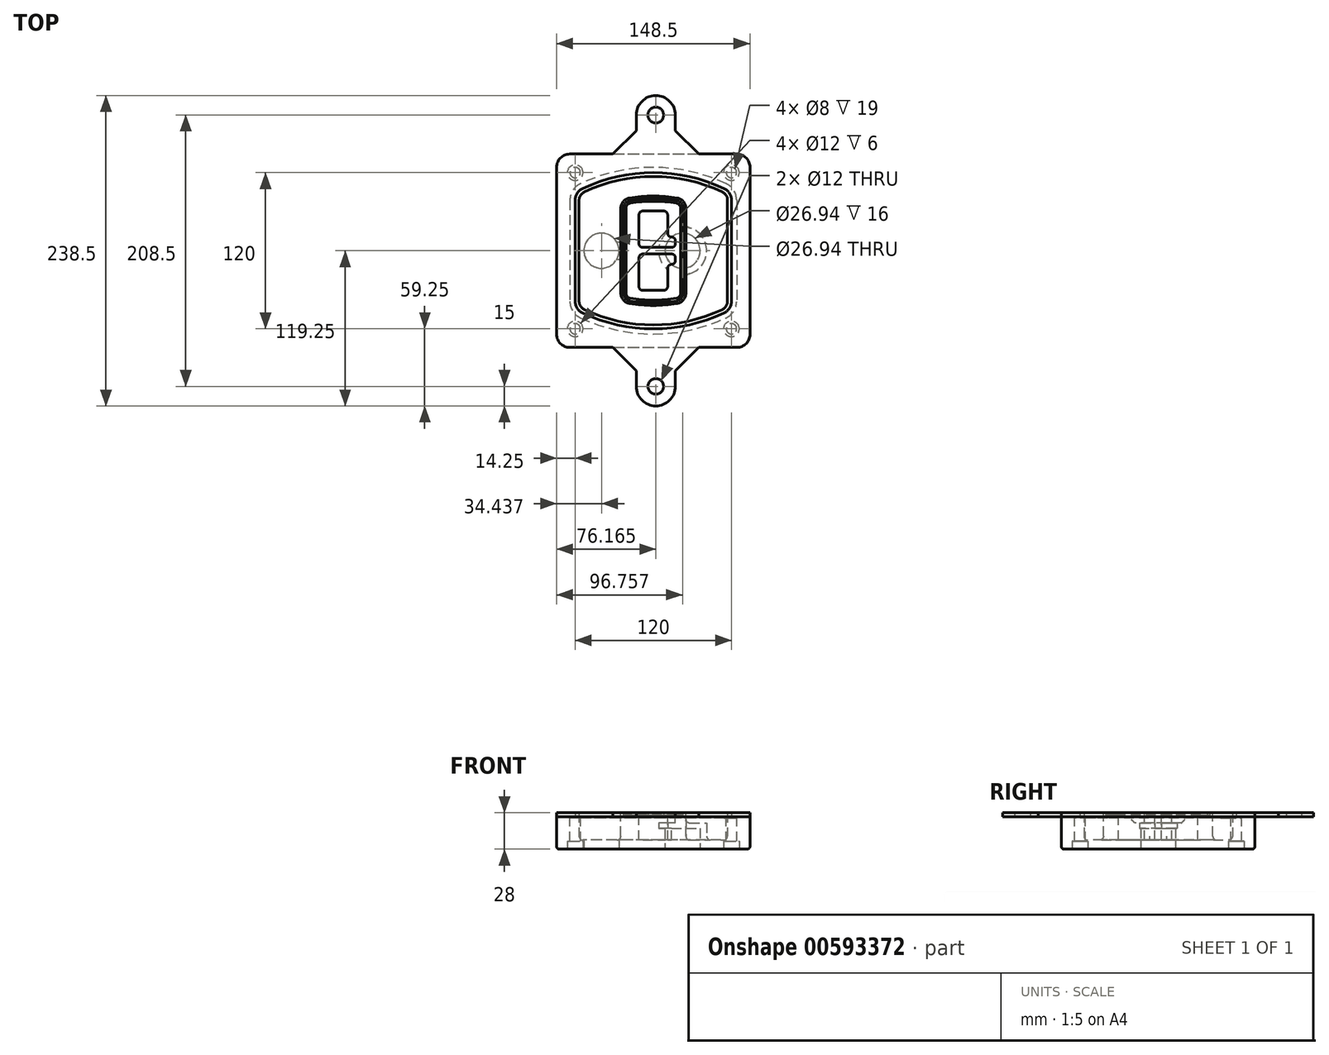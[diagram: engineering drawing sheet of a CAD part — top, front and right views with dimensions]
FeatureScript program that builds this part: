
annotation { "Feature Type Name" : "Feature", "Feature Type Description" : "" }
export const myFeature = defineFeature(function(context is Context, id is Id, definition is map)
    precondition{}
    {
        {
            var Q0;
            Q0=qCreatedBy(makeId("Top.planeOp"),FACE);
            var sketch = newSketch(context, id + "F0", { "sketchPlane" : qUnion([Q0])});
            skPoint(sketch, "E0.rect.middle", {"position": v(0, 0) * mm});
            skLineSegment(sketch, "E1.bottom", {"start": v(-64.25, -74.25) * mm, "end": v(64.25, -74.25) * mm});
            skLineSegment(sketch, "E1.top", {"start": v(-64.25, 74.25) * mm, "end": v(64.25, 74.25) * mm});
            skLineSegment(sketch, "E1.left", {"start": v(-74.25, -64.25) * mm, "end": v(-74.25, 64.25) * mm});
            skLineSegment(sketch, "E1.right", {"start": v(74.25, -64.25) * mm, "end": v(74.25, 64.25) * mm});
            skLineSegment(sketch, "E2", {"start": v(-74.25, 74.25) * mm, "end": v(74.25, -74.25) * mm, "construction": true});
            skLineSegment(sketch, "E3", {"start": v(74.25, 74.25) * mm, "end": v(-74.25, -74.25) * mm, "construction": true});
            skCircle(sketch, "E4", {"center": v(-60, 60) * mm, "radius": 4 * mm});
            skCircle(sketch, "E5", {"center": v(60, 60) * mm, "radius": 4 * mm});
            skCircle(sketch, "E6", {"center": v(60, -60) * mm, "radius": 4 * mm});
            skCircle(sketch, "E7", {"center": v(-60, -60) * mm, "radius": 4 * mm});
            skLineSegment(sketch, "E8", {"start": v(-60, 60) * mm, "end": v(60, 60) * mm, "construction": true});
            skLineSegment(sketch, "E9", {"start": v(60, 60) * mm, "end": v(60, -60) * mm, "construction": true});
            skLineSegment(sketch, "E10", {"start": v(60, -60) * mm, "end": v(-60, -60) * mm, "construction": true});
            skLineSegment(sketch, "E11", {"start": v(-60, -60) * mm, "end": v(-60, 60) * mm, "construction": true});
            skLineSegment(sketch, "E12", {"start": v(-60, 38.83) * mm, "end": v(-60, -38.83) * mm});
            skLineSegment(sketch, "E13", {"start": v(60, 38.83) * mm, "end": v(60, -38.83) * mm});
            skArc(sketch, "E14", {"start": v(54.26, 47.88) * mm, "mid": v(0, 60) * mm, "end": v(-54.26, 47.88) * mm});
            skArc(sketch, "E15", {"start": v(-54.26, -47.88) * mm, "mid": v(0, -60) * mm, "end": v(54.26, -47.88) * mm});
            skLineSegment(sketch, "E16", {"start": v(-60, 0) * mm, "end": v(60, 0) * mm, "construction": true});
            skPoint(sketch, "E17.visualSharp", {"position": v(-60, -45) * mm});
            skArc(sketch, "E17.filletArc", {"start": v(-60, -38.83) * mm, "mid": v(-58.44, -44.2) * mm, "end": v(-54.26, -47.88) * mm});
            skPoint(sketch, "E18.visualSharp", {"position": v(-60, 45) * mm});
            skArc(sketch, "E18.filletArc", {"start": v(-54.26, 47.88) * mm, "mid": v(-58.44, 44.2) * mm, "end": v(-60, 38.83) * mm});
            skPoint(sketch, "E19.visualSharp", {"position": v(60, 45) * mm});
            skArc(sketch, "E19.filletArc", {"start": v(60, 38.83) * mm, "mid": v(58.44, 44.2) * mm, "end": v(54.26, 47.88) * mm});
            skPoint(sketch, "E20.visualSharp", {"position": v(60, -45) * mm});
            skArc(sketch, "E20.filletArc", {"start": v(54.26, -47.88) * mm, "mid": v(58.44, -44.2) * mm, "end": v(60, -38.83) * mm});
            skPoint(sketch, "E21.visualSharp", {"position": v(-74.25, 74.25) * mm});
            skArc(sketch, "E21.filletArc", {"start": v(-64.25, 74.25) * mm, "mid": v(-71.32, 71.32) * mm, "end": v(-74.25, 64.25) * mm});
            skPoint(sketch, "E22.visualSharp", {"position": v(74.25, 74.25) * mm});
            skArc(sketch, "E22.filletArc", {"start": v(74.25, 64.25) * mm, "mid": v(71.32, 71.32) * mm, "end": v(64.25, 74.25) * mm});
            skPoint(sketch, "E23.visualSharp", {"position": v(74.25, -74.25) * mm});
            skArc(sketch, "E23.filletArc", {"start": v(64.25, -74.25) * mm, "mid": v(71.32, -71.32) * mm, "end": v(74.25, -64.25) * mm});
            skPoint(sketch, "E24.visualSharp", {"position": v(-74.25, -74.25) * mm});
            skArc(sketch, "E24.filletArc", {"start": v(-74.25, -64.25) * mm, "mid": v(-71.32, -71.32) * mm, "end": v(-64.25, -74.25) * mm});
            skArc(sketch, "E25.0", {"start": v(57, 38.83) * mm, "mid": v(55.9, 42.58) * mm, "end": v(52.98, 45.17) * mm});
            skLineSegment(sketch, "E25.1", {"start": v(57, 38.83) * mm, "end": v(57, -38.83) * mm});
            skArc(sketch, "E25.2", {"start": v(52.98, -45.17) * mm, "mid": v(55.9, -42.58) * mm, "end": v(57, -38.83) * mm});
            skArc(sketch, "E25.3", {"start": v(-52.98, -45.17) * mm, "mid": v(0, -57) * mm, "end": v(52.98, -45.17) * mm});
            skArc(sketch, "E25.4", {"start": v(-57, -38.83) * mm, "mid": v(-55.9, -42.58) * mm, "end": v(-52.98, -45.17) * mm});
            skArc(sketch, "E25.5", {"start": v(52.98, 45.17) * mm, "mid": v(0, 57) * mm, "end": v(-52.98, 45.17) * mm});
            skLineSegment(sketch, "E25.6", {"start": v(-57, 38.83) * mm, "end": v(-57, -38.83) * mm});
            skArc(sketch, "E25.7", {"start": v(-52.98, 45.17) * mm, "mid": v(-55.9, 42.58) * mm, "end": v(-57, 38.83) * mm});
            skArc(sketch, "E26.0", {"start": v(-55.96, 51.5) * mm, "mid": v(-61.82, 46.33) * mm, "end": v(-64, 38.83) * mm});
            skArc(sketch, "E26.1", {"start": v(55.96, 51.5) * mm, "mid": v(0, 64) * mm, "end": v(-55.96, 51.5) * mm});
            skArc(sketch, "E26.2", {"start": v(64, 38.83) * mm, "mid": v(61.82, 46.33) * mm, "end": v(55.96, 51.5) * mm});
            skLineSegment(sketch, "E26.3", {"start": v(64, 38.83) * mm, "end": v(64, -38.83) * mm});
            skArc(sketch, "E26.4", {"start": v(55.96, -51.5) * mm, "mid": v(61.82, -46.33) * mm, "end": v(64, -38.83) * mm});
            skLineSegment(sketch, "E26.5", {"start": v(-64, 38.83) * mm, "end": v(-64, -38.83) * mm});
            skArc(sketch, "E26.6", {"start": v(-55.96, -51.5) * mm, "mid": v(0, -64) * mm, "end": v(55.96, -51.5) * mm});
            skArc(sketch, "E26.7", {"start": v(-64, -38.83) * mm, "mid": v(-61.82, -46.33) * mm, "end": v(-55.96, -51.5) * mm});
            skSolve(sketch);
        }
        {
            var Q0;
            Q0=makeQuery(id+"F0.imprint","IMPRINT",FACE,{"disambiguationData":[TD([[makeQuery(id+"F0.imprint","IMPRINT",EDGE,{"derivedFrom":sQuery(id+"F0.wireOp",EDGE,"E1.bottom")}),1.0]])]});
            var Q1;
            Q1=makeQuery(id+"F0.imprint","IMPRINT",FACE,{"disambiguationData":[TD([[makeQuery(id+"F0.imprint","IMPRINT",EDGE,{"derivedFrom":sQuery(id+"F0.wireOp",EDGE,"E12")}),1.0]])]});
            var Q2;
            Q2=makeQuery(id+"F0.imprint","IMPRINT",FACE,{"disambiguationData":[TD([[makeQuery(id+"F0.imprint","IMPRINT",EDGE,{"derivedFrom":sQuery(id+"F0.wireOp",EDGE,"E25.0")}),1.0]])]});
            var Q3;
            Q3=makeQuery(id+"F0.imprint","IMPRINT",FACE,{"disambiguationData":[TD([[makeQuery(id+"F0.imprint","IMPRINT",EDGE,{"derivedFrom":sQuery(id+"F0.wireOp",EDGE,"E12")}),-1.0]])]});
            extrude(context, id + "F1", {"entities" : qUnion([Q0, Q1, Q2, Q3]), "oppositeDirection" : true, "depth" : 25 * mm});
        }
        {
            var Q0;
            Q0=makeQuery(id+"F0.imprint","IMPRINT",FACE,{"disambiguationData":[TD([[makeQuery(id+"F0.imprint","IMPRINT",EDGE,{"derivedFrom":sQuery(id+"F0.wireOp",EDGE,"E12")}),1.0]])]});
            extrude(context, id + "F2", {"entities" : qUnion([Q0]), "operationType" : NewBodyOperationType.ADD, "depth" : 3 * mm});
        }
        {
            var Q0;
            Q0=makeQuery(id+"F0.imprint","IMPRINT",FACE,{"disambiguationData":[TD([[makeQuery(id+"F0.imprint","IMPRINT",EDGE,{"derivedFrom":sQuery(id+"F0.wireOp",EDGE,"E12")}),-1.0]])]});
            extrude(context, id + "F3", {"entities" : qUnion([Q0]), "operationType" : NewBodyOperationType.REMOVE, "oppositeDirection" : true, "depth" : 1 * mm});
        }
        {
            var Q0;
            Q0=makeQuery(id+"F0.imprint","IMPRINT",FACE,{"disambiguationData":[TD([[makeQuery(id+"F0.imprint","IMPRINT",EDGE,{"derivedFrom":sQuery(id+"F0.wireOp",EDGE,"E25.0")}),1.0]])]});
            extrude(context, id + "F4", {"entities" : qUnion([Q0]), "operationType" : NewBodyOperationType.REMOVE, "oppositeDirection" : true, "depth" : 18 * mm});
        }
        {
            var Q0;
            Q0=makeQuery(id+"F2.opExtrude","CAP_FACE",FACE,{"disambiguationData":[OSD([sQuery(id+"F0.wireOp",EDGE,"E12"),sQuery(id+"F0.wireOp",EDGE,"E13"),sQuery(id+"F0.wireOp",EDGE,"E14"),sQuery(id+"F0.wireOp",EDGE,"E15"),sQuery(id+"F0.wireOp",EDGE,"E17.filletArc"),sQuery(id+"F0.wireOp",EDGE,"E18.filletArc"),sQuery(id+"F0.wireOp",EDGE,"E19.filletArc"),sQuery(id+"F0.wireOp",EDGE,"E20.filletArc"),sQuery(id+"F0.wireOp",EDGE,"E25.0"),sQuery(id+"F0.wireOp",EDGE,"E25.1"),sQuery(id+"F0.wireOp",EDGE,"E25.2"),sQuery(id+"F0.wireOp",EDGE,"E25.3"),sQuery(id+"F0.wireOp",EDGE,"E25.4"),sQuery(id+"F0.wireOp",EDGE,"E25.5"),sQuery(id+"F0.wireOp",EDGE,"E25.6"),sQuery(id+"F0.wireOp",EDGE,"E25.7")])],"isStart":false});
            var sketch = newSketch(context, id + "F5", { "sketchPlane" : qUnion([Q0])});
            skArc(sketch, "E27.0", {"start": v(-18.34, -40.45) * mm, "mid": v(0, -42) * mm, "end": v(18.34, -40.45) * mm});
            skArc(sketch, "E28.0", {"start": v(18.34, 40.45) * mm, "mid": v(0, 42) * mm, "end": v(-18.34, 40.45) * mm});
            skLineSegment(sketch, "E29", {"start": v(-25, 32.57) * mm, "end": v(-25, -32.57) * mm});
            skLineSegment(sketch, "E30", {"start": v(25, 32.57) * mm, "end": v(25, -32.57) * mm});
            skLineSegment(sketch, "E31", {"start": v(-25, 39.1) * mm, "end": v(25, 39.1) * mm, "construction": true});
            skLineSegment(sketch, "E32", {"start": v(-25, -39.1) * mm, "end": v(25, -39.1) * mm, "construction": true});
            skPoint(sketch, "E33.visualSharp", {"position": v(-25, 39.1) * mm});
            skArc(sketch, "E33.filletArc", {"start": v(-18.34, 40.45) * mm, "mid": v(-23.11, 37.73) * mm, "end": v(-25, 32.57) * mm});
            skPoint(sketch, "E34.visualSharp", {"position": v(25, 39.1) * mm});
            skArc(sketch, "E34.filletArc", {"start": v(25, 32.57) * mm, "mid": v(23.11, 37.73) * mm, "end": v(18.34, 40.45) * mm});
            skPoint(sketch, "E35.visualSharp", {"position": v(25, -39.1) * mm});
            skArc(sketch, "E35.filletArc", {"start": v(18.34, -40.45) * mm, "mid": v(23.11, -37.73) * mm, "end": v(25, -32.57) * mm});
            skPoint(sketch, "E36.visualSharp", {"position": v(-25, -39.1) * mm});
            skArc(sketch, "E36.filletArc", {"start": v(-25, -32.57) * mm, "mid": v(-23.11, -37.73) * mm, "end": v(-18.34, -40.45) * mm});
            skArc(sketch, "E37.0", {"start": v(52.98, 45.17) * mm, "mid": v(0, 57) * mm, "end": v(-52.98, 45.17) * mm});
            skArc(sketch, "E37.1", {"start": v(-52.98, 45.17) * mm, "mid": v(-55.9, 42.58) * mm, "end": v(-57, 38.83) * mm});
            skLineSegment(sketch, "E37.2", {"start": v(-57, 38.83) * mm, "end": v(-57, -38.83) * mm});
            skArc(sketch, "E37.3", {"start": v(-57, -38.83) * mm, "mid": v(-55.9, -42.58) * mm, "end": v(-52.98, -45.17) * mm});
            skArc(sketch, "E37.4", {"start": v(-52.98, -45.17) * mm, "mid": v(0, -57) * mm, "end": v(52.98, -45.17) * mm});
            skArc(sketch, "E37.5", {"start": v(52.98, -45.17) * mm, "mid": v(55.9, -42.58) * mm, "end": v(57, -38.83) * mm});
            skLineSegment(sketch, "E37.6", {"start": v(57, 38.83) * mm, "end": v(57, -38.83) * mm});
            skArc(sketch, "E37.7", {"start": v(57, 38.83) * mm, "mid": v(55.9, 42.58) * mm, "end": v(52.98, 45.17) * mm});
            skLineSegment(sketch, "E38.0", {"start": v(23, 32.57) * mm, "end": v(23, -32.57) * mm});
            skArc(sketch, "E38.1", {"start": v(18, -38.48) * mm, "mid": v(21.58, -36.44) * mm, "end": v(23, -32.57) * mm});
            skArc(sketch, "E38.2", {"start": v(-18, -38.48) * mm, "mid": v(0, -40) * mm, "end": v(18, -38.48) * mm});
            skArc(sketch, "E38.3", {"start": v(-23, -32.57) * mm, "mid": v(-21.58, -36.44) * mm, "end": v(-18, -38.48) * mm});
            skLineSegment(sketch, "E38.4", {"start": v(-23, 32.57) * mm, "end": v(-23, -32.57) * mm});
            skArc(sketch, "E38.5", {"start": v(23, 32.57) * mm, "mid": v(21.58, 36.44) * mm, "end": v(18, 38.48) * mm});
            skArc(sketch, "E38.6", {"start": v(-18, 38.48) * mm, "mid": v(-21.58, 36.44) * mm, "end": v(-23, 32.57) * mm});
            skArc(sketch, "E38.7", {"start": v(18, 38.48) * mm, "mid": v(0, 40) * mm, "end": v(-18, 38.48) * mm});
            skArc(sketch, "E39.0", {"start": v(21, 32.57) * mm, "mid": v(20.06, 35.15) * mm, "end": v(17.67, 36.5) * mm});
            skLineSegment(sketch, "E39.1", {"start": v(21, 32.57) * mm, "end": v(21, -32.57) * mm});
            skArc(sketch, "E39.2", {"start": v(17.67, -36.5) * mm, "mid": v(20.06, -35.15) * mm, "end": v(21, -32.57) * mm});
            skArc(sketch, "E39.3", {"start": v(-17.67, -36.5) * mm, "mid": v(0, -38) * mm, "end": v(17.67, -36.5) * mm});
            skArc(sketch, "E39.4", {"start": v(-21, -32.57) * mm, "mid": v(-20.06, -35.15) * mm, "end": v(-17.67, -36.5) * mm});
            skArc(sketch, "E39.5", {"start": v(17.67, 36.5) * mm, "mid": v(0, 38) * mm, "end": v(-17.67, 36.5) * mm});
            skLineSegment(sketch, "E39.6", {"start": v(-21, 32.57) * mm, "end": v(-21, -32.57) * mm});
            skArc(sketch, "E39.7", {"start": v(-17.67, 36.5) * mm, "mid": v(-20.06, 35.15) * mm, "end": v(-21, 32.57) * mm});
            skLineSegment(sketch, "E40", {"start": v(-25, 0) * mm, "end": v(25, 0) * mm, "construction": true});
            skLineSegment(sketch, "E41", {"start": v(-11, 5.5) * mm, "end": v(-11, 27.5) * mm});
            skLineSegment(sketch, "E42", {"start": v(-8, 30.5) * mm, "end": v(8, 30.5) * mm});
            skLineSegment(sketch, "E43", {"start": v(11, 27.5) * mm, "end": v(11, 13.5) * mm});
            skLineSegment(sketch, "E44", {"start": v(14, 10.5) * mm, "end": v(14, 10.5) * mm});
            skLineSegment(sketch, "E45", {"start": v(17, 7.5) * mm, "end": v(17, 5.5) * mm});
            skLineSegment(sketch, "E46", {"start": v(14, 2.5) * mm, "end": v(-8, 2.5) * mm});
            skPoint(sketch, "E47.visualSharp", {"position": v(-11, 30.5) * mm});
            skArc(sketch, "E47.filletArc", {"start": v(-8, 30.5) * mm, "mid": v(-10.12, 29.62) * mm, "end": v(-11, 27.5) * mm});
            skPoint(sketch, "E48.visualSharp", {"position": v(11, 30.5) * mm});
            skArc(sketch, "E48.filletArc", {"start": v(11, 27.5) * mm, "mid": v(10.12, 29.62) * mm, "end": v(8, 30.5) * mm});
            skPoint(sketch, "E49.visualSharp", {"position": v(11, 10.5) * mm});
            skArc(sketch, "E49.filletArc", {"start": v(11, 13.5) * mm, "mid": v(11.88, 11.38) * mm, "end": v(14, 10.5) * mm});
            skPoint(sketch, "E50.visualSharp", {"position": v(17, 10.5) * mm});
            skArc(sketch, "E50.filletArc", {"start": v(17, 7.5) * mm, "mid": v(16.12, 9.62) * mm, "end": v(14, 10.5) * mm});
            skPoint(sketch, "E51.visualSharp", {"position": v(17, 2.5) * mm});
            skArc(sketch, "E51.filletArc", {"start": v(14, 2.5) * mm, "mid": v(16.12, 3.38) * mm, "end": v(17, 5.5) * mm});
            skPoint(sketch, "E52.visualSharp", {"position": v(-11, 2.5) * mm});
            skArc(sketch, "E52.filletArc", {"start": v(-11, 5.5) * mm, "mid": v(-10.12, 3.38) * mm, "end": v(-8, 2.5) * mm});
            skLineSegment(sketch, "E53.0.MirrorCS", {"start": v(14, -2.5) * mm, "end": v(-8, -2.5) * mm});
            skArc(sketch, "E54.0.MirrorCS", {"start": v(-11, -5.5) * mm, "mid": v(-10.12, -3.38) * mm, "end": v(-8, -2.5) * mm});
            skLineSegment(sketch, "E55.0.MirrorCS", {"start": v(-11, -5.5) * mm, "end": v(-11, -27.5) * mm});
            skArc(sketch, "E56.0.MirrorCS", {"start": v(-8, -30.5) * mm, "mid": v(-10.12, -29.62) * mm, "end": v(-11, -27.5) * mm});
            skLineSegment(sketch, "E57.0.MirrorCS", {"start": v(-8, -30.5) * mm, "end": v(8, -30.5) * mm});
            skArc(sketch, "E58.0.MirrorCS", {"start": v(11, -27.5) * mm, "mid": v(10.12, -29.62) * mm, "end": v(8, -30.5) * mm});
            skLineSegment(sketch, "E59.0.MirrorCS", {"start": v(11, -27.5) * mm, "end": v(11, -13.5) * mm});
            skArc(sketch, "E60.0.MirrorCS", {"start": v(11, -13.5) * mm, "mid": v(11.88, -11.38) * mm, "end": v(14, -10.5) * mm});
            skArc(sketch, "E61.0.MirrorCS", {"start": v(17, -7.5) * mm, "mid": v(16.12, -9.62) * mm, "end": v(14, -10.5) * mm});
            skLineSegment(sketch, "E62.0.MirrorCS", {"start": v(17, -7.5) * mm, "end": v(17, -5.5) * mm});
            skArc(sketch, "E63.0.MirrorCS", {"start": v(14, -2.5) * mm, "mid": v(16.12, -3.38) * mm, "end": v(17, -5.5) * mm});
            skSolve(sketch);
        }
        {
            var Q0;
            Q0=makeQuery(id+"F5.imprint","IMPRINT",FACE,{"disambiguationData":[TD([[makeQuery(id+"F5.imprint","IMPRINT",EDGE,{"derivedFrom":sQuery(id+"F5.wireOp",EDGE,"E27.0")}),1.0]])]});
            var Q1;
            Q1=makeQuery(id+"F5.imprint","IMPRINT",FACE,{"disambiguationData":[TD([[makeQuery(id+"F5.imprint","IMPRINT",EDGE,{"derivedFrom":sQuery(id+"F5.wireOp",EDGE,"E38.0")}),-1.0]])]});
            var Q2;
            Q2=makeQuery(id+"F5.imprint","IMPRINT",FACE,{"disambiguationData":[TD([[makeQuery(id+"F5.imprint","IMPRINT",EDGE,{"derivedFrom":sQuery(id+"F5.wireOp",EDGE,"E39.0")}),1.0]])]});
            extrude(context, id + "F6", {"entities" : qUnion([Q0, Q1, Q2]), "operationType" : NewBodyOperationType.ADD, "endBound" : BoundingType.UP_TO_NEXT, "oppositeDirection" : true, "depth" : 25 * mm});
        }
        {
            var Q0;
            Q0=makeQuery(id+"F5.imprint","IMPRINT",FACE,{"disambiguationData":[TD([[makeQuery(id+"F5.imprint","IMPRINT",EDGE,{"derivedFrom":sQuery(id+"F5.wireOp",EDGE,"E38.0")}),-1.0]])]});
            extrude(context, id + "F7", {"entities" : qUnion([Q0]), "operationType" : NewBodyOperationType.REMOVE, "oppositeDirection" : true, "depth" : 2 * mm});
        }
        {
            var Q0;
            Q0=makeQuery(id+"F1.opExtrude","CAP_FACE",FACE,{"disambiguationData":[OSD([sQuery(id+"F0.wireOp",EDGE,"E1.bottom"),sQuery(id+"F0.wireOp",EDGE,"E1.top"),sQuery(id+"F0.wireOp",EDGE,"E1.left"),sQuery(id+"F0.wireOp",EDGE,"E1.right"),sQuery(id+"F0.wireOp",EDGE,"E4"),sQuery(id+"F0.wireOp",EDGE,"E5"),sQuery(id+"F0.wireOp",EDGE,"E6"),sQuery(id+"F0.wireOp",EDGE,"E7"),sQuery(id+"F0.wireOp",EDGE,"E21.filletArc"),sQuery(id+"F0.wireOp",EDGE,"E22.filletArc"),sQuery(id+"F0.wireOp",EDGE,"E23.filletArc"),sQuery(id+"F0.wireOp",EDGE,"E24.filletArc")])],"isStart":false});
            var sketch = newSketch(context, id + "F8", { "sketchPlane" : qUnion([Q0])});
            skCircle(sketch, "E64", {"center": v(22.5, 0) * mm, "radius": 13.47 * mm});
            skCircle(sketch, "E65", {"center": v(-39.81, 0) * mm, "radius": 13.47 * mm});
            skLineSegment(sketch, "E66", {"start": v(74.25, 0) * mm, "end": v(-74.25, 0) * mm});
            skCircle(sketch, "E67", {"center": v(22.5, 0) * mm, "radius": 18.47 * mm});
            skCircle(sketch, "E68", {"center": v(60, -60) * mm, "radius": 6 * mm});
            skCircle(sketch, "E69", {"center": v(-60, -60) * mm, "radius": 6 * mm});
            skCircle(sketch, "E70", {"center": v(-60, 60) * mm, "radius": 6 * mm});
            skCircle(sketch, "E71", {"center": v(60, 60) * mm, "radius": 6 * mm});
            skSolve(sketch);
        }
        {
            var Q0;
            {var subQ1=sQuery(id+"F8.wireOp",EDGE,"E66");var subQ4=sQuery(id+"F8.wireOp",EDGE,"E64");var subQ6=makeQuery(id+"F8.imprint","INTERSECT",VERTEX,{"disambiguationData":[OD(0.0)],"derivedFrom":[subQ4,subQ1]});Q0=makeQuery(id+"F8.imprint","IMPRINT",FACE,{"disambiguationData":[TD([[makeQuery(id+"F8.imprint","IMPRINT",EDGE,{"disambiguationData":[TD([[subQ6,-1.0]])],"derivedFrom":subQ4}),-1.0]])]});}
            var Q1;
            {var subQ0=sQuery(id+"F8.wireOp",EDGE,"E66");var subQ1=sQuery(id+"F8.wireOp",EDGE,"E64");var subQ3=makeQuery(id+"F8.imprint","INTERSECT",VERTEX,{"disambiguationData":[OD(0.0)],"derivedFrom":[subQ1,subQ0]});Q1=makeQuery(id+"F8.imprint","IMPRINT",FACE,{"disambiguationData":[TD([[makeQuery(id+"F8.imprint","IMPRINT",EDGE,{"disambiguationData":[TD([[subQ3,-1.0]])],"derivedFrom":subQ1}),1.0]])]});}
            var Q2;
            {var subQ0=sQuery(id+"F8.wireOp",EDGE,"E66");var subQ1=sQuery(id+"F8.wireOp",EDGE,"E64");var subQ3=makeQuery(id+"F8.imprint","INTERSECT",VERTEX,{"disambiguationData":[OD(0.0)],"derivedFrom":[subQ1,subQ0]});Q2=makeQuery(id+"F8.imprint","IMPRINT",FACE,{"disambiguationData":[TD([[makeQuery(id+"F8.imprint","IMPRINT",EDGE,{"disambiguationData":[TD([[subQ3,1.0]])],"derivedFrom":subQ1}),1.0]])]});}
            var Q3;
            {var subQ1=sQuery(id+"F8.wireOp",EDGE,"E66");var subQ4=sQuery(id+"F8.wireOp",EDGE,"E64");var subQ6=makeQuery(id+"F8.imprint","INTERSECT",VERTEX,{"disambiguationData":[OD(0.0)],"derivedFrom":[subQ4,subQ1]});Q3=makeQuery(id+"F8.imprint","IMPRINT",FACE,{"disambiguationData":[TD([[makeQuery(id+"F8.imprint","IMPRINT",EDGE,{"disambiguationData":[TD([[subQ6,1.0]])],"derivedFrom":subQ4}),-1.0]])]});}
            extrude(context, id + "F9", {"entities" : qUnion([Q0, Q1, Q2, Q3]), "operationType" : NewBodyOperationType.ADD, "oppositeDirection" : true, "depth" : 20 * mm});
        }
        {
            var Q0;
            {var subQ0=sQuery(id+"F8.wireOp",EDGE,"E66");var subQ1=sQuery(id+"F8.wireOp",EDGE,"E64");var subQ3=makeQuery(id+"F8.imprint","INTERSECT",VERTEX,{"disambiguationData":[OD(0.0)],"derivedFrom":[subQ1,subQ0]});Q0=makeQuery(id+"F8.imprint","IMPRINT",FACE,{"disambiguationData":[TD([[makeQuery(id+"F8.imprint","IMPRINT",EDGE,{"disambiguationData":[TD([[subQ3,-1.0]])],"derivedFrom":subQ1}),1.0]])]});}
            var Q1;
            {var subQ0=sQuery(id+"F8.wireOp",EDGE,"E66");var subQ1=sQuery(id+"F8.wireOp",EDGE,"E64");var subQ3=makeQuery(id+"F8.imprint","INTERSECT",VERTEX,{"disambiguationData":[OD(0.0)],"derivedFrom":[subQ1,subQ0]});Q1=makeQuery(id+"F8.imprint","IMPRINT",FACE,{"disambiguationData":[TD([[makeQuery(id+"F8.imprint","IMPRINT",EDGE,{"disambiguationData":[TD([[subQ3,1.0]])],"derivedFrom":subQ1}),1.0]])]});}
            extrude(context, id + "F10", {"entities" : qUnion([Q0, Q1]), "operationType" : NewBodyOperationType.REMOVE, "oppositeDirection" : true, "depth" : 16 * mm});
        }
        {
            var Q0;
            {var subQ0=sQuery(id+"F8.wireOp",EDGE,"E66");var subQ1=sQuery(id+"F8.wireOp",EDGE,"E65");var subQ3=makeQuery(id+"F8.imprint","INTERSECT",VERTEX,{"disambiguationData":[OD(0.0)],"derivedFrom":[subQ1,subQ0]});Q0=makeQuery(id+"F8.imprint","IMPRINT",FACE,{"disambiguationData":[TD([[makeQuery(id+"F8.imprint","IMPRINT",EDGE,{"disambiguationData":[TD([[subQ3,-1.0]])],"derivedFrom":subQ1}),1.0]])]});}
            var Q1;
            {var subQ0=sQuery(id+"F8.wireOp",EDGE,"E66");var subQ1=sQuery(id+"F8.wireOp",EDGE,"E65");var subQ3=makeQuery(id+"F8.imprint","INTERSECT",VERTEX,{"disambiguationData":[OD(0.0)],"derivedFrom":[subQ1,subQ0]});Q1=makeQuery(id+"F8.imprint","IMPRINT",FACE,{"disambiguationData":[TD([[makeQuery(id+"F8.imprint","IMPRINT",EDGE,{"disambiguationData":[TD([[subQ3,1.0]])],"derivedFrom":subQ1}),1.0]])]});}
            extrude(context, id + "F11", {"entities" : qUnion([Q0, Q1]), "operationType" : NewBodyOperationType.REMOVE, "oppositeDirection" : true, "depth" : 25 * mm});
        }
        {
            var Q0;
            Q0=makeQuery(id+"F8.imprint","IMPRINT",FACE,{"disambiguationData":[TD([[makeQuery(id+"F8.imprint","IMPRINT",EDGE,{"derivedFrom":sQuery(id+"F8.wireOp",EDGE,"E68")}),1.0]])]});
            var Q1;
            Q1=makeQuery(id+"F8.imprint","IMPRINT",FACE,{"disambiguationData":[TD([[makeQuery(id+"F8.imprint","IMPRINT",EDGE,{"derivedFrom":makeQuery(id+"F1.opExtrude","CAP_EDGE",EDGE,{"disambiguationData":[OSD([sQuery(id+"F0.wireOp",EDGE,"E5")])],"isStart":false})}),-1.0]])]});
            var Q2;
            Q2=makeQuery(id+"F8.imprint","IMPRINT",FACE,{"disambiguationData":[TD([[makeQuery(id+"F8.imprint","IMPRINT",EDGE,{"derivedFrom":sQuery(id+"F8.wireOp",EDGE,"E69")}),1.0]])]});
            var Q3;
            Q3=makeQuery(id+"F8.imprint","IMPRINT",FACE,{"disambiguationData":[TD([[makeQuery(id+"F8.imprint","IMPRINT",EDGE,{"derivedFrom":makeQuery(id+"F1.opExtrude","CAP_EDGE",EDGE,{"disambiguationData":[OSD([sQuery(id+"F0.wireOp",EDGE,"E4")])],"isStart":false})}),-1.0]])]});
            var Q4;
            Q4=makeQuery(id+"F8.imprint","IMPRINT",FACE,{"disambiguationData":[TD([[makeQuery(id+"F8.imprint","IMPRINT",EDGE,{"derivedFrom":sQuery(id+"F8.wireOp",EDGE,"E70")}),1.0]])]});
            var Q5;
            Q5=makeQuery(id+"F8.imprint","IMPRINT",FACE,{"disambiguationData":[TD([[makeQuery(id+"F8.imprint","IMPRINT",EDGE,{"derivedFrom":makeQuery(id+"F1.opExtrude","CAP_EDGE",EDGE,{"disambiguationData":[OSD([sQuery(id+"F0.wireOp",EDGE,"E7")])],"isStart":false})}),-1.0]])]});
            var Q6;
            Q6=makeQuery(id+"F8.imprint","IMPRINT",FACE,{"disambiguationData":[TD([[makeQuery(id+"F8.imprint","IMPRINT",EDGE,{"derivedFrom":sQuery(id+"F8.wireOp",EDGE,"E71")}),1.0]])]});
            var Q7;
            Q7=makeQuery(id+"F8.imprint","IMPRINT",FACE,{"disambiguationData":[TD([[makeQuery(id+"F8.imprint","IMPRINT",EDGE,{"derivedFrom":makeQuery(id+"F1.opExtrude","CAP_EDGE",EDGE,{"disambiguationData":[OSD([sQuery(id+"F0.wireOp",EDGE,"E6")])],"isStart":false})}),-1.0]])]});
            extrude(context, id + "F12", {"entities" : qUnion([Q0, Q1, Q2, Q3, Q4, Q5, Q6, Q7]), "operationType" : NewBodyOperationType.REMOVE, "oppositeDirection" : true, "depth" : 6 * mm});
        }
        {
            var Q0;
            Q0=makeQuery(id+"F10.boolean.opBoolean","COPY",FACE,{"derivedFrom":makeQuery(id+"F10.opExtrude","CAP_FACE",FACE,{"disambiguationData":[OSD([sQuery(id+"F8.wireOp",EDGE,"E64")])],"isStart":false})});
            var sketch = newSketch(context, id + "F13", { "sketchPlane" : qUnion([Q0])});
            skArc(sketch, "E72.0", {"start": v(11, 14.45) * mm, "mid": v(6.45, 9.13) * mm, "end": v(4.2, 2.5) * mm});
            skArc(sketch, "E72.1", {"start": v(4.2, -2.5) * mm, "mid": v(6.45, -9.13) * mm, "end": v(11, -14.45) * mm});
            skLineSegment(sketch, "E73", {"start": v(4.2, -2.5) * mm, "end": v(14, -2.5) * mm});
            skLineSegment(sketch, "E74.0", {"start": v(14, 2.5) * mm, "end": v(4.2, 2.5) * mm});
            skArc(sketch, "E74.1", {"start": v(14, 2.5) * mm, "mid": v(16.12, 3.38) * mm, "end": v(17, 5.5) * mm});
            skLineSegment(sketch, "E74.2", {"start": v(17, 7.5) * mm, "end": v(17, 5.5) * mm});
            skArc(sketch, "E74.3", {"start": v(17, 7.5) * mm, "mid": v(16.12, 9.62) * mm, "end": v(14, 10.5) * mm});
            skArc(sketch, "E74.4", {"start": v(11, 13.5) * mm, "mid": v(11.88, 11.38) * mm, "end": v(14, 10.5) * mm});
            skLineSegment(sketch, "E74.5", {"start": v(11, 14.45) * mm, "end": v(11, 13.5) * mm});
            skLineSegment(sketch, "E74.7", {"start": v(14, -2.5) * mm, "end": v(4.2, -2.5) * mm});
            skArc(sketch, "E74.8", {"start": v(14, -2.5) * mm, "mid": v(16.12, -3.38) * mm, "end": v(17, -5.5) * mm});
            skLineSegment(sketch, "E74.9", {"start": v(17, -7.5) * mm, "end": v(17, -5.5) * mm});
            skArc(sketch, "E74.10", {"start": v(17, -7.5) * mm, "mid": v(16.12, -9.62) * mm, "end": v(14, -10.5) * mm});
            skArc(sketch, "E74.11", {"start": v(11, -13.5) * mm, "mid": v(11.88, -11.38) * mm, "end": v(14, -10.5) * mm});
            skLineSegment(sketch, "E74.12", {"start": v(11, -14.45) * mm, "end": v(11, -13.5) * mm});
            skPoint(sketch, "E75.orphan", {"position": v(11, -27.5) * mm});
            skPoint(sketch, "E76.orphan", {"position": v(-8, -2.5) * mm});
            skPoint(sketch, "E77.orphan", {"position": v(-8, 2.5) * mm});
            skPoint(sketch, "E78.orphan", {"position": v(11, 27.5) * mm});
            skSolve(sketch);
        }
        {
            var Q0;
            {var subQ7=sQuery(id+"F13.wireOp",EDGE,"E72.0");var subQ14=sQuery(id+"F13.wireOp",EDGE,"E72.1");var subQ16=sQuery(id+"F13.wireOp",EDGE,"E74.1");var subQ18=sQuery(id+"F13.wireOp",EDGE,"E74.8");Q0=qUnion([makeQuery(id+"F13.imprint","IMPRINT",FACE,{"disambiguationData":[TD([[makeQuery(id+"F13.imprint","IMPRINT",EDGE,{"derivedFrom":subQ7}),1.0]])]}),makeQuery(id+"F13.imprint","IMPRINT",FACE,{"disambiguationData":[TD([[makeQuery(id+"F13.imprint","IMPRINT",EDGE,{"derivedFrom":subQ14}),1.0]])]}),makeQuery(id+"F13.imprint","IMPRINT",FACE,{"disambiguationData":[TD([[makeQuery(id+"F13.imprint","IMPRINT",EDGE,{"derivedFrom":subQ16}),1.0]])]}),makeQuery(id+"F13.imprint","IMPRINT",FACE,{"disambiguationData":[TD([[makeQuery(id+"F13.imprint","IMPRINT",EDGE,{"derivedFrom":subQ18}),-1.0]])]})]);}
            var Q1;
            Q1=makeQuery(id+"F6.boolean.opBoolean","SPLIT",FACE,{"disambiguationData":[TD([makeQuery(id+"F6.opExtrude","SWEPT_FACE",FACE,{"disambiguationData":[OSD([sQuery(id+"F5.wireOp",EDGE,"E41")])]})])],"derivedFrom":makeQuery(id+"F4.boolean.opBoolean","COPY",FACE,{"derivedFrom":makeQuery(id+"F4.opExtrude","CAP_FACE",FACE,{"disambiguationData":[OSD([sQuery(id+"F0.wireOp",EDGE,"E25.0"),sQuery(id+"F0.wireOp",EDGE,"E25.1"),sQuery(id+"F0.wireOp",EDGE,"E25.2"),sQuery(id+"F0.wireOp",EDGE,"E25.3"),sQuery(id+"F0.wireOp",EDGE,"E25.4"),sQuery(id+"F0.wireOp",EDGE,"E25.5"),sQuery(id+"F0.wireOp",EDGE,"E25.6"),sQuery(id+"F0.wireOp",EDGE,"E25.7")])],"isStart":false})})});
            extrude(context, id + "F14", {"entities" : qUnion([Q0]), "operationType" : NewBodyOperationType.REMOVE, "endBound" : BoundingType.UP_TO_SURFACE, "endBoundEntityFace" : qUnion([Q1]), "depth" : 25 * mm});
        }
        {
            var Q0;
            Q0=makeQuery(id+"F4.boolean.opBoolean","COPY",EDGE,{"derivedFrom":makeQuery(id+"F4.opExtrude","CAP_EDGE",EDGE,{"disambiguationData":[OSD([sQuery(id+"F0.wireOp",EDGE,"E25.6")])],"isStart":false})});
            var Q1;
            Q1=makeQuery(id+"F9.boolean.opBoolean","INTERSECT",EDGE,{"derivedFrom":[makeQuery(id+"F6.opExtrude","SWEPT_FACE",FACE,{"disambiguationData":[OSD([sQuery(id+"F5.wireOp",EDGE,"E30")])]}),makeQuery(id+"F9.opExtrude","CAP_FACE",FACE,{"disambiguationData":[OSD([sQuery(id+"F8.wireOp",EDGE,"E67")])],"isStart":false})]});
            var Q2;
            Q2=makeQuery(id+"F9.boolean.opBoolean","INTERSECT",EDGE,{"disambiguationData":[OD(1.0)],"derivedFrom":[makeQuery(id+"F6.opExtrude","SWEPT_FACE",FACE,{"disambiguationData":[OSD([sQuery(id+"F5.wireOp",EDGE,"E30")])]}),makeQuery(id+"F9.opExtrude","SWEPT_FACE",FACE,{"disambiguationData":[OSD([sQuery(id+"F8.wireOp",EDGE,"E67")])]})]});
            var Q3;
            {var subQ0=sQuery(id+"F5.wireOp",EDGE,"E30");Q3=makeQuery(id+"F9.boolean.opBoolean","SPLIT",EDGE,{"disambiguationData":[TD([makeQuery(id+"F6.opExtrude","SWEPT_FACE",FACE,{"disambiguationData":[OSD([sQuery(id+"F5.wireOp",EDGE,"E35.filletArc")])]})])],"derivedFrom":makeQuery(id+"F6.opExtrude","CAP_EDGE",EDGE,{"disambiguationData":[OSD([subQ0])],"isStart":false})});}
            var Q4;
            {var subQ0=sQuery(id+"F0.wireOp",EDGE,"E25.7");var subQ1=sQuery(id+"F0.wireOp",EDGE,"E25.6");var subQ2=sQuery(id+"F0.wireOp",EDGE,"E25.5");var subQ3=sQuery(id+"F0.wireOp",EDGE,"E25.4");var subQ4=sQuery(id+"F0.wireOp",EDGE,"E25.0");var subQ5=sQuery(id+"F0.wireOp",EDGE,"E25.1");var subQ6=sQuery(id+"F0.wireOp",EDGE,"E25.2");var subQ7=sQuery(id+"F0.wireOp",EDGE,"E25.3");Q4=makeQuery(id+"F9.boolean.opBoolean","INTERSECT",EDGE,{"derivedFrom":[makeQuery(id+"F6.boolean.opBoolean","SPLIT",FACE,{"disambiguationData":[TD([makeQuery(id+"F2.opExtrude","SWEPT_FACE",FACE,{"disambiguationData":[OSD([subQ4])]})])],"derivedFrom":makeQuery(id+"F4.boolean.opBoolean","COPY",FACE,{"derivedFrom":makeQuery(id+"F4.opExtrude","CAP_FACE",FACE,{"disambiguationData":[OSD([subQ4,subQ5,subQ6,subQ7,subQ3,subQ2,subQ1,subQ0])],"isStart":false})})}),makeQuery(id+"F9.opExtrude","SWEPT_FACE",FACE,{"disambiguationData":[OSD([sQuery(id+"F8.wireOp",EDGE,"E67")])]})]});}
            var Q5;
            Q5=makeQuery(id+"F9.boolean.opBoolean","INTERSECT",EDGE,{"disambiguationData":[OD(0.0)],"derivedFrom":[makeQuery(id+"F6.opExtrude","SWEPT_FACE",FACE,{"disambiguationData":[OSD([sQuery(id+"F5.wireOp",EDGE,"E30")])]}),makeQuery(id+"F9.opExtrude","SWEPT_FACE",FACE,{"disambiguationData":[OSD([sQuery(id+"F8.wireOp",EDGE,"E67")])]})]});
            fillet(context, id + "F15", {"entities" : qUnion([Q0, Q1, Q2, Q3, Q4, Q5]), "radius" : 3 * mm, "tangentPropagation" : true, "allowEdgeOverflow" : false});
        }
        {
            var Q0;
            Q0=makeQuery(id+"F1.opExtrude","CAP_EDGE",EDGE,{"disambiguationData":[OSD([sQuery(id+"F0.wireOp",EDGE,"E1.bottom")])],"isStart":false});
            fillet(context, id + "F16", {"entities" : qUnion([Q0]), "radius" : 2 * mm, "tangentPropagation" : true, "allowEdgeOverflow" : false});
        }
        {
            var Q0;
            {var subQ0=sQuery(id+"F0.wireOp",EDGE,"E21.filletArc");var subQ1=sQuery(id+"F0.wireOp",EDGE,"E7");var subQ2=sQuery(id+"F0.wireOp",EDGE,"E6");var subQ3=sQuery(id+"F0.wireOp",EDGE,"E5");var subQ4=sQuery(id+"F0.wireOp",EDGE,"E4");var subQ5=sQuery(id+"F0.wireOp",EDGE,"E22.filletArc");var subQ6=sQuery(id+"F0.wireOp",EDGE,"E1.bottom");var subQ7=sQuery(id+"F0.wireOp",EDGE,"E1.right");var subQ8=sQuery(id+"F0.wireOp",EDGE,"E1.top");var subQ9=sQuery(id+"F0.wireOp",EDGE,"E1.left");var subQ10=sQuery(id+"F0.wireOp",EDGE,"E23.filletArc");var subQ11=sQuery(id+"F0.wireOp",EDGE,"E24.filletArc");Q0=makeQuery(id+"F2.boolean.opBoolean","SPLIT",FACE,{"disambiguationData":[TD([makeQuery(id+"F1.opExtrude","SWEPT_FACE",FACE,{"disambiguationData":[OSD([subQ6])]})])],"derivedFrom":makeQuery(id+"F1.opExtrude","CAP_FACE",FACE,{"disambiguationData":[OSD([subQ6,subQ8,subQ9,subQ7,subQ4,subQ3,subQ2,subQ1,subQ0,subQ5,subQ10,subQ11])],"isStart":true})});}
            var sketch = newSketch(context, id + "F17", { "sketchPlane" : qUnion([Q0])});
            skLineSegment(sketch, "E79.0.0", {"start": v(64.25, 74.25) * mm, "end": v(-64.25, 74.25) * mm});
            skArc(sketch, "E79.0.1", {"start": v(-64.25, 74.25) * mm, "mid": v(-71.32, 71.32) * mm, "end": v(-74.25, 64.25) * mm});
            skLineSegment(sketch, "E79.0.2", {"start": v(-74.25, 64.25) * mm, "end": v(-74.25, -64.25) * mm});
            skArc(sketch, "E79.0.3", {"start": v(-74.25, -64.25) * mm, "mid": v(-71.32, -71.32) * mm, "end": v(-64.25, -74.25) * mm});
            skLineSegment(sketch, "E79.0.4", {"start": v(-64.25, -74.25) * mm, "end": v(64.25, -74.25) * mm});
            skArc(sketch, "E79.0.5", {"start": v(64.25, -74.25) * mm, "mid": v(71.32, -71.32) * mm, "end": v(74.25, -64.25) * mm});
            skLineSegment(sketch, "E79.0.6", {"start": v(74.25, -64.25) * mm, "end": v(74.25, 64.25) * mm});
            skArc(sketch, "E79.0.7", {"start": v(74.25, 64.25) * mm, "mid": v(71.32, 71.32) * mm, "end": v(64.25, 74.25) * mm});
            skLineSegment(sketch, "E80", {"start": v(1.91, 74.25) * mm, "end": v(1.91, 104.25) * mm, "construction": true});
            skCircle(sketch, "E81", {"center": v(1.91, 104.25) * mm, "radius": 6 * mm});
            skArc(sketch, "E82", {"start": v(16.91, 104.25) * mm, "mid": v(1.91, 119.25) * mm, "end": v(-13.09, 104.25) * mm});
            skLineSegment(sketch, "E83", {"start": v(-13.09, 104.25) * mm, "end": v(-13.09, 92.25) * mm});
            skLineSegment(sketch, "E84", {"start": v(16.91, 104.25) * mm, "end": v(16.91, 92.25) * mm});
            skLineSegment(sketch, "E85", {"start": v(-13.09, 92.25) * mm, "end": v(-31.09, 74.25) * mm});
            skLineSegment(sketch, "E86", {"start": v(16.91, 92.25) * mm, "end": v(34.91, 74.25) * mm});
            skLineSegment(sketch, "E87.MirrorCS", {"start": v(-13.09, -92.25) * mm, "end": v(-31.09, -74.25) * mm});
            skLineSegment(sketch, "E88.MirrorCS", {"start": v(-13.09, -104.25) * mm, "end": v(-13.09, -92.25) * mm});
            skArc(sketch, "E89.MirrorCS", {"start": v(16.91, -104.25) * mm, "mid": v(1.91, -119.25) * mm, "end": v(-13.09, -104.25) * mm});
            skCircle(sketch, "E90.MirrorC", {"center": v(1.91, -104.25) * mm, "radius": 6 * mm});
            skLineSegment(sketch, "E91.MirrorCS", {"start": v(1.91, -74.25) * mm, "end": v(1.91, -104.25) * mm, "construction": true});
            skLineSegment(sketch, "E92.MirrorCS", {"start": v(16.91, -104.25) * mm, "end": v(16.91, -92.25) * mm});
            skLineSegment(sketch, "E93.MirrorCS", {"start": v(16.91, -92.25) * mm, "end": v(34.91, -74.25) * mm});
            skSolve(sketch);
        }
        {
            var Q0;
            Q0 = qSketchRegion(id + "F17", true);
            var Q1;
            Q1=makeQuery(id+"F2.opExtrude","CAP_FACE",FACE,{"disambiguationData":[OSD([sQuery(id+"F0.wireOp",EDGE,"E12"),sQuery(id+"F0.wireOp",EDGE,"E13"),sQuery(id+"F0.wireOp",EDGE,"E14"),sQuery(id+"F0.wireOp",EDGE,"E15"),sQuery(id+"F0.wireOp",EDGE,"E17.filletArc"),sQuery(id+"F0.wireOp",EDGE,"E18.filletArc"),sQuery(id+"F0.wireOp",EDGE,"E19.filletArc"),sQuery(id+"F0.wireOp",EDGE,"E20.filletArc"),sQuery(id+"F0.wireOp",EDGE,"E25.0"),sQuery(id+"F0.wireOp",EDGE,"E25.1"),sQuery(id+"F0.wireOp",EDGE,"E25.2"),sQuery(id+"F0.wireOp",EDGE,"E25.3"),sQuery(id+"F0.wireOp",EDGE,"E25.4"),sQuery(id+"F0.wireOp",EDGE,"E25.5"),sQuery(id+"F0.wireOp",EDGE,"E25.6"),sQuery(id+"F0.wireOp",EDGE,"E25.7")])],"isStart":false});
            extrude(context, id + "F18", {"entities" : qUnion([Q0]), "endBound" : BoundingType.UP_TO_SURFACE, "depth" : 25 * mm, "endBoundEntityFace" : qUnion([Q1]), "offsetDistance" : 25 * mm});
        }
    });
